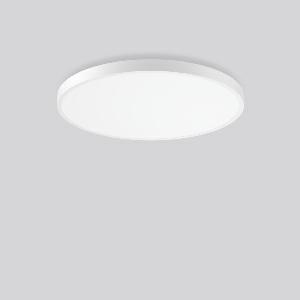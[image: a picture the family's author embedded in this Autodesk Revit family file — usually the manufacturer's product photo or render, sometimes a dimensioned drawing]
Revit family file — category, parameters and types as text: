
# Revit family: triona_round_a_312388_002_730_c8b9
name_source: partatom
category: Lighting Fixtures
units: mm (PartAtom-declared; Revit-internal decimal feet)

## family parameters
Cut with Voids When Loaded = No
Host = Face
Light Source = No
Part Type = Normal
Room Calculation Point = No
Round Connector Dimension = Use Diameter
Shared = No

## types (1)
- TRIONA round A (1 x LED Modul 830, 12400 lm, 3000)
    Apparent Load = 133 VA
    CIE Flux Codes = 49 80 96 71 100
    Color Rendering = 80
    Color Temperature = 3000
    Default Elevation = 1800 mm
    Description = Series: TRIONA round
Decorative round LED surface-mounted luminaire. Flat, seamless frame: aluminium extrusion profile, powder coated. Cover made of sheet steel, powder-coated. Direct light emission through a diffuser plastic opal. Indirect light emission through a flush diffuser made of satin-finish plastic. Lightguide and diffuser made of non-yellowing plastic (PMMA). Lateral light emission (RZB SIDELITE technology) for above-average homogeneous light distribution. Direct 70%, indirect 30% light emission. Suitable for Ceiling mounting, Wall (surface). Tool-free mounting via bayonet connection. Electronic ballast included. Very easy installation thanks to Plug+Play connection. With Casambi smart+free Bluetooth control for wireless network and operation using Android / iOS devices, free app available for download. 
Colour: traffic white, matt (RAL 9016)
Diameter: 845 mm
Height: 88 mm
Lamp: LED
Socket: without socket
Colour temperature: 3000K
Colour rendering index (CRI): 80
System power: 133 W
Rated luminous flux: 12400 lm
Luminous efficiency: 93 lm/W
Control gear: Dimmable Bluetooth converter
Protection class: I
Type of protection: IP 20
    Height = 88 mm
    Lamp = 1 x LED Modul 830
    Lamp Light Flux = 12400 lm
    Lamp count = 1
    Length = 845 mm
    Lifetime = 50000 h
    Luminous efficacy = 93 lm/W
    Manufacturer = RZB
    ModVariant = No
    Model = 312388.002.730
    Mounting Place = Ceiling
    Mounting Type = Surface mounted
    Number of Poles = 1
    OnlyDefault = Yes
    Power Factor = 1
    Product Name = TRIONA round A
    Product group = Surface mounted modular luminaires
    ProductGroupID = 306
    Protection Class = Protection class I
    Protection Degree = IP 20
    RLX_Detail_Level = 1
    RLX_Emergency_Light_Flux = 0 lm
    RLX_Emergency_Type = 0
    RLX_Emergency_Type_DB = No
    RlxData = <blob elided: 41129 chars, md5=c0d03d4f>
    Socket = socket
    Standby Power = 0 W
    System Light Flux = 12400 lm
    System Power = 133 W
    Type Comments = Product without accessories
    Type Image = 312388.002.jpg
    URL = http://relux.com
    VarID = ---
    Voltage = 230 V
    Voltage Range = 220-240 V
    Weight = 0.00 kg
    Width = 0 mm  [stored 0 ft]

note: [stored X ft] marks values corroborated as IEEE doubles in the binary element streams (Revit-internal decimal feet)

## geometry (parser evidence)
native form markers: Blend x4, Sweep x13
no freeform markers — native parametric forms only
